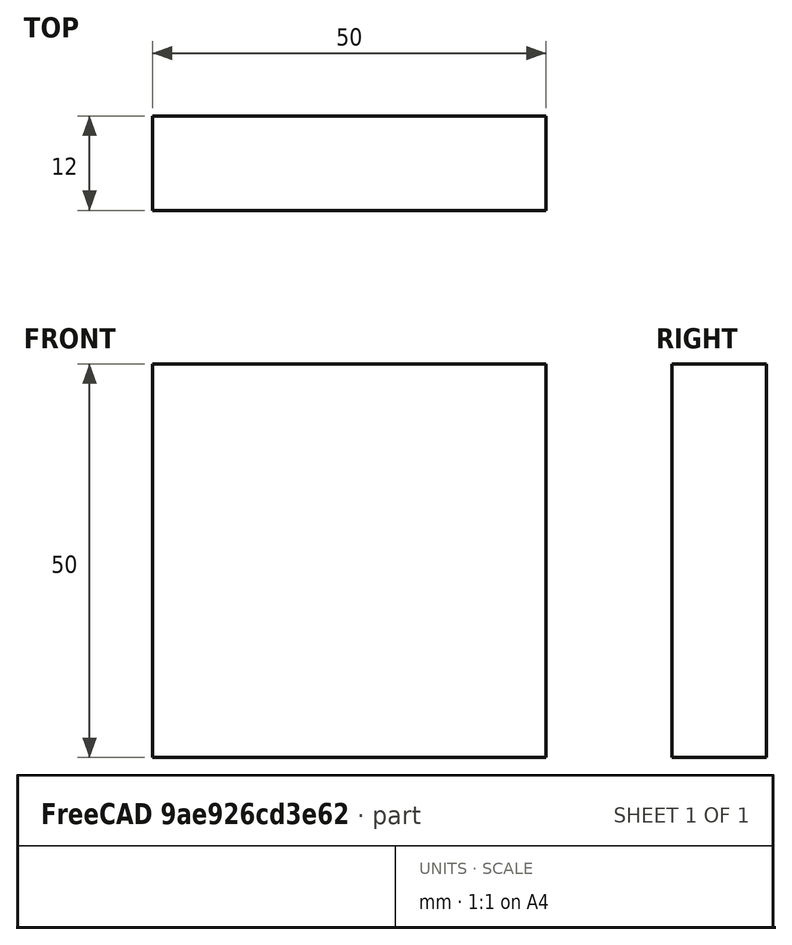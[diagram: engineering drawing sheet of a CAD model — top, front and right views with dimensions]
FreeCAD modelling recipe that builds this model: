
FCSTD DOCUMENT  (FreeCAD 0.15R4671 (Git))
Label: Flat Bar 50x12 EN10058 S235JR
License: All rights reserved
LicenseURL: http://en.wikipedia.org/wiki/All_rights_reserved
objects: Sketcher::SketchObject×1, Part::Extrusion×1
note: 2 computed .brp shape members not serialized (recipe doc carries the construction recipe); baked Part::Feature solids carry a one-line shape summary decoded from their .brp

FEATURE [Sketcher::SketchObject] Sketch
  sketch-geometry (4):
    g0: LineSegment StartX=-25 StartY=-6 StartZ=0 EndX=25 EndY=-6 EndZ=0
    g1: LineSegment StartX=25 StartY=-6 StartZ=0 EndX=25 EndY=6 EndZ=0
    g2: LineSegment StartX=25 StartY=6 StartZ=0 EndX=-25 EndY=6 EndZ=0
    g3: LineSegment StartX=-25 StartY=6 StartZ=0 EndX=-25 EndY=-6 EndZ=0
  constraints (12):
    c: Coincident(g0,g1)
    c: Coincident(g1,g2)
    c: Coincident(g2,g3)
    c: Coincident(g3,g0)
    c: Horizontal(g0)
    c: Horizontal(g2)
    c: Vertical(g1)
    c: Vertical(g3)
    c: Symmetric(g1,g2,g-2)
    c: Symmetric(g0,g1,g-1)
    c: DistanceY(g1) = 12
    c: DistanceX(g0) = 50
FEATURE [Part::Extrusion] Extrude  label="Flat Bar 50x12 EN10058 S235JR"
  Base = -> Sketch
  Dir = (0,0,50)
  Solid = true
